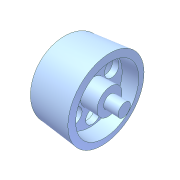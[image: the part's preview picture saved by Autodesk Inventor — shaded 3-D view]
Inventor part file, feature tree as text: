
AUTODESK INVENTOR PART (.ipt)
format: ipt  version: unknown  size: 227,328 bytes
history: native  units: in
note: dims shown in document units (in); Inventor stores cm internally (conversion verified against a paired STEP export)
features: sketch x3, revolve x2, extrude x1, pattern_circular x1
ambient origin geometry x8: Origin, YZ Plane, XZ Plane, XY Plane, X Axis, Y Axis, Z Axis, Center Point
feature tree (7):
  revolve  "Revolution1"  [1 undecoded]
  extrude  "Extrusion3"  Depth=0.0394in
  pattern_circular  "Circular Pattern3"  [2 undecoded]
  revolve  "Revolution2"  [1 undecoded]
  sketch  "Sketch1"  dims[d0=0.2362in d2=0.2756in d4=0.0394in]
  sketch  "Sketch4"  dims[d5=90.0deg d24=0.0394in]
  sketch  "Sketch5"  dims[d25=0.0394in d34=0.0197in d35=0.1181in d39=0.1378in d40=0.0984in d41=0.3937in d42=0.0in d43=2.3622in d44=360.0deg d46=0.0in d47=0.0787in d48=0.0787in d49=0.0394in d50=90.0deg d51=0.1181in d52=0.3937in d53=0.0787in]
note: 4 required parameter values undecoded (feature->parameter linkage not recoverable at this tier; creation-order binding heuristic only, values carry confidence <= 0.55)